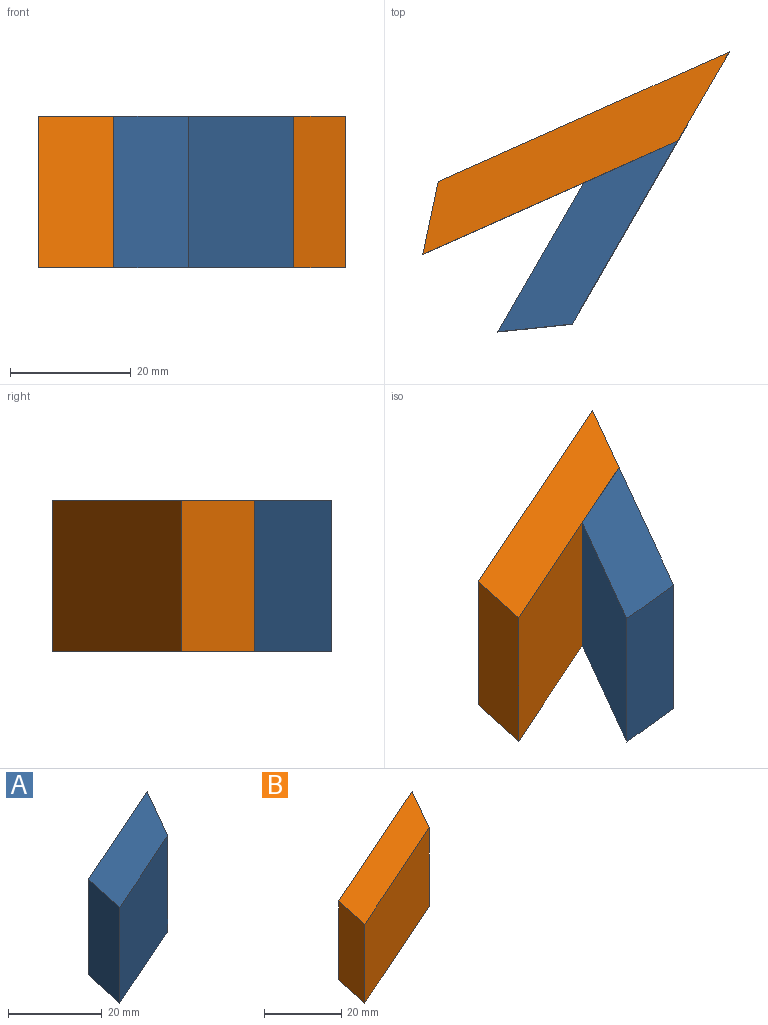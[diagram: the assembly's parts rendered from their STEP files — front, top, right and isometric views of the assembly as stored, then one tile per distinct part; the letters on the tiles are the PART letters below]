
ASSEMBLY  parts=2 mates=1
PART A: 6 faces, bbox 34.5x26.3x25 mm
  f0: plane 26.04x25mm, normal (0.41,-0.91,0), area 712.5mm2, adj f1,f3,f4,f5
  f1: plane 25x14.73mm, normal (0.87,-0.5,0), area 425.3mm2, adj f0,f2,f4,f5
  f2: plane 31.97x25mm, normal (-0.41,0.91,0), area 875mm2, adj f1,f3,f4,f5
  f3: plane 25x12.09mm, normal (-0.98,0.21,0), area 309mm2, adj f0,f2,f4,f5
  f4: plane 34.54x26.33mm, normal (0,0,1), area 317.5mm2, adj f0,f1,f2,f3
  f5: plane 34.54x26.33mm, normal (0,0,-1), area 317.5mm2, adj f0,f1,f2,f3
PART B: 6 faces, bbox 50.7x33.5x25 mm
  f0: plane 25x12.09mm, normal (-0.98,0.21,0), area 309mm2, adj f1,f3,f4,f5
  f1: plane 42.24x25mm, normal (0.41,-0.91,0), area 1155.9mm2, adj f0,f2,f4,f5
  f2: plane 25x14.73mm, normal (0.87,-0.5,0), area 425.3mm2, adj f1,f3,f4,f5
  f3: plane 48.18x25mm, normal (-0.41,0.91,0), area 1318.4mm2, adj f0,f2,f4,f5
  f4: plane 50.75x33.54mm, normal (0,0,1), area 494.9mm2, adj f0,f1,f2,f3
  f5: plane 50.75x33.54mm, normal (0,0,-1), area 494.9mm2, adj f0,f1,f2,f3
PLACE A rot(axis=(-0.74,-0.67,0),180deg) t=(-33.97,9.88,25)mm
PLACE B t=(3.23,-7.26,0)mm
MATE fastened A.f2 <-> B.f2  axis (0.87,-0.5,0) through (14.13,24.33,12.5)mm
